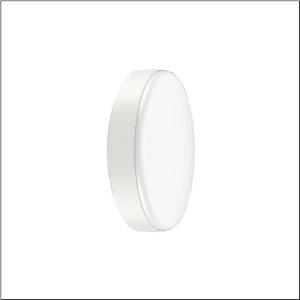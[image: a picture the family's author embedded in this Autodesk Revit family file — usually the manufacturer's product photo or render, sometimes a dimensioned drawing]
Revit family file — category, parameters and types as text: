
# Revit family: rondel_31_51wc10mb34a
name_source: partatom
category: Lighting Fixtures
units: mm (PartAtom-declared; Revit-internal decimal feet)

## family parameters
Cut with Voids When Loaded = No
Host = Face
Light Source = No
Part Type = Normal
Room Calculation Point = No
Round Connector Dimension = Use Diameter
Shared = No

## types (1)
- --- (1 x LED, 4250 lm, 34 W, 3000K)
    Apparent Load = 34 VA
    CIE Flux Codes = 44 75 94 94 100
    Color Rendering = 80
    Color Temperature = 3000K
    Default Elevation = 1800 mm
    Description = Rondel 31, wall and ceiling luminaire, primary optical cover: cover, of PC, opal, light emission: direct distribution, primary light characteristic: symmetric, installation type: surface-mounted, LED, rated luminous flux: 4.250lm, luminous efficacy: 125lm/W, light colour: 830, colour temperature: 3000K, with terminal, 3-pole, max. 2.5mm², mains connection: 220..240V, AC, 50/60Hz, rated input power: 34W, luminaire housing, of PC, traffic white (RAL 9016), diameter: 480mm, protection rating (complete): IP65, insulation class (complete): insulation class II (safety insulation), certification: CE, impact resistance: IK10, permissible operating ambient temperature: -20..+40°C, permissible storage temperature: -20..+60°C, packaging unit: 1 piece
    Height = 97 mm
    Lamp = 1 x LED
    Lamp Light Flux = 4250 lm
    Lamp Power = 34 W
    Lamp count = 1
    Length = 480 mm
    Luminous efficacy = 125 lm/W
    Manufacturer = Siteco
    ModVariant = No
    Model = 51WC10MB34A
    Mounting Place = Ceiling
    Mounting Type = Surface mounted
    Number of Poles = 1
    OnlyDefault = Yes
    Power Factor = 1
    Product Name = Rondel 31
    Product group = wall and ceiling luminaire
    ProductGroupID = 302
    Protection Class = Protection class II
    Protection Degree = IP 65
    RLX_Detail_Level = 1
    RLX_Emergency_Light_Flux = 0 lm
    RLX_Emergency_Type = 0
    RLX_Emergency_Type_DB = No
    RlxData = <blob elided: 41473 chars, md5=6f221758>
    Socket = socket
    Standby Power = 0 W
    System Light Flux = 4250 lm
    System Power = 34 W
    Type Comments = factory setting: luminous flux: 100 % | (ON | ON)
    Type Image = l_1007188.jpg
    URL = http://relux.com
    VarID = @adj_101021
    Voltage = 0 V
    Weight = 0.00 kg
    Width = 0 mm  [stored 0 ft]

note: [stored X ft] marks values corroborated as IEEE doubles in the binary element streams (Revit-internal decimal feet)

## geometry (parser evidence)
native form markers: Blend x4, Sweep x13
no freeform markers — native parametric forms only
